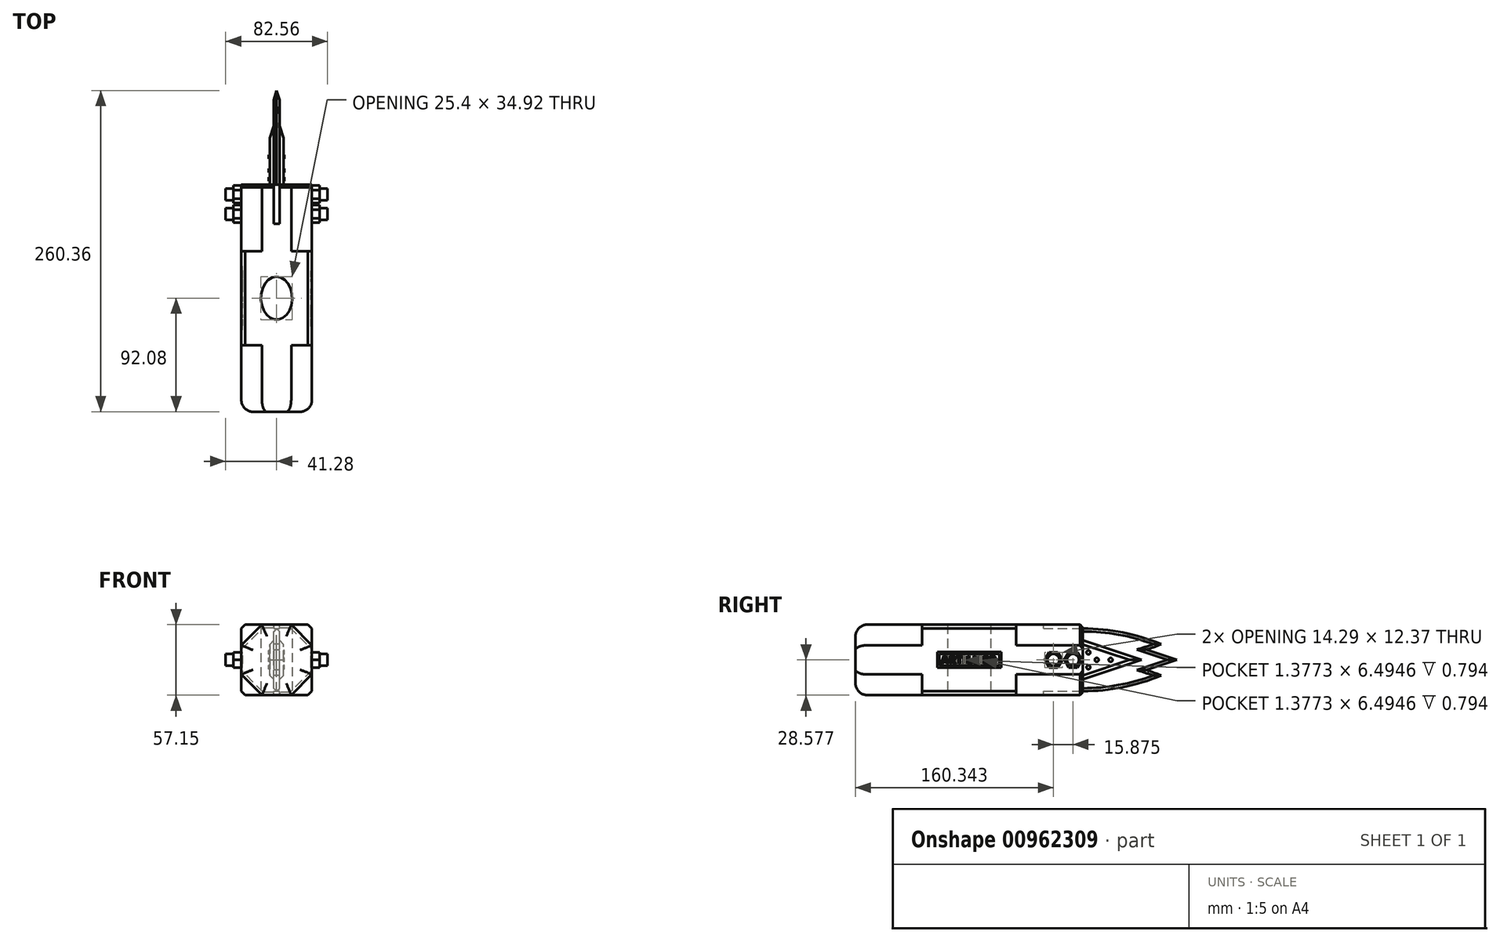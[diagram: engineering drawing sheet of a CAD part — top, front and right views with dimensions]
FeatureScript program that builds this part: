
annotation { "Feature Type Name" : "Feature", "Feature Type Description" : "" }
export const myFeature = defineFeature(function(context is Context, id is Id, definition is map)
    precondition{}
    {
        {
            var Q0;
            Q0=qCreatedBy(makeId("Top.planeOp"),FACE);
            var sketch = newSketch(context, id + "F0", { "sketchPlane" : qUnion([Q0])});
            skEllipse(sketch, "E0", {"center": v(0, 0) * mm, "majorRadius": 12.7 * mm, "minorRadius": 17.46 * mm, "majorAxis": v(1, 0)});
            skSolve(sketch);
        }
        {
            var Q0;
            Q0=qSketchRegion(id+"F0",true);
            extrude(context, id + "F1", {"entities" : qUnion([Q0]), "depth" : 1219.2 * mm, "offsetDistance" : 25.4 * mm});
        }
        {
            var Q0;
            Q0=qCreatedBy(makeId("Front.planeOp"),FACE);
            var sketch = newSketch(context, id + "F2", { "sketchPlane" : qUnion([Q0])});
            skCircle(sketch, "E1.cCircle", {"center": v(0, 1177.87) * mm, "radius": 30.93 * mm, "construction": true});
            skLineSegment(sketch, "E1.0", {"start": v(28.57, 1189.7) * mm, "end": v(28.57, 1166.03) * mm});
            skLineSegment(sketch, "E1.1", {"start": v(28.57, 1166.03) * mm, "end": v(11.84, 1149.3) * mm});
            skLineSegment(sketch, "E1.2", {"start": v(11.84, 1149.3) * mm, "end": v(-11.84, 1149.3) * mm});
            skLineSegment(sketch, "E1.3", {"start": v(-11.84, 1149.3) * mm, "end": v(-28.58, 1166.03) * mm});
            skLineSegment(sketch, "E1.4", {"start": v(-28.58, 1166.03) * mm, "end": v(-28.58, 1189.7) * mm});
            skLineSegment(sketch, "E1.5", {"start": v(-28.57, 1189.7) * mm, "end": v(-11.84, 1206.44) * mm});
            skLineSegment(sketch, "E1.6", {"start": v(-11.84, 1206.44) * mm, "end": v(11.84, 1206.44) * mm});
            skLineSegment(sketch, "E1.7", {"start": v(11.84, 1206.44) * mm, "end": v(28.57, 1189.7) * mm});
            skLineSegment(sketch, "E2.bottom", {"start": v(28.57, 1206.44) * mm, "end": v(-28.58, 1206.44) * mm});
            skLineSegment(sketch, "E2.top", {"start": v(28.57, 1149.3) * mm, "end": v(-28.58, 1149.3) * mm});
            skLineSegment(sketch, "E2.left", {"start": v(28.57, 1206.44) * mm, "end": v(28.57, 1149.3) * mm});
            skLineSegment(sketch, "E2.right", {"start": v(-28.58, 1206.44) * mm, "end": v(-28.58, 1149.3) * mm});
            skSolve(sketch);
        }
        {
            var Q0;
            {var subQ0=sQuery(id+"F2.wireOp",EDGE,"E1.5");Q0=makeQuery(id+"F2.imprint","IMPRINT",FACE,{"disambiguationData":[TD([[makeQuery(id+"F2.imprint","IMPRINT",EDGE,{"derivedFrom":subQ0}),1.0]])]});}
            var Q1;
            {var subQ0=sQuery(id+"F2.wireOp",EDGE,"E1.7");Q1=makeQuery(id+"F2.imprint","IMPRINT",FACE,{"disambiguationData":[TD([[makeQuery(id+"F2.imprint","IMPRINT",EDGE,{"derivedFrom":subQ0}),1.0]])]});}
            var Q2;
            Q2=makeQuery(id+"F2.imprint","IMPRINT",FACE,{"disambiguationData":[TD([[makeQuery(id+"F2.imprint","IMPRINT",EDGE,{"derivedFrom":sQuery(id+"F2.wireOp",EDGE,"E1.0")}),-1.0]])]});
            var Q3;
            {var subQ0=sQuery(id+"F2.wireOp",EDGE,"E1.3");Q3=makeQuery(id+"F2.imprint","IMPRINT",FACE,{"disambiguationData":[TD([[makeQuery(id+"F2.imprint","IMPRINT",EDGE,{"derivedFrom":subQ0}),1.0]])]});}
            var Q4;
            {var subQ0=sQuery(id+"F2.wireOp",EDGE,"E1.1");Q4=makeQuery(id+"F2.imprint","IMPRINT",FACE,{"disambiguationData":[TD([[makeQuery(id+"F2.imprint","IMPRINT",EDGE,{"derivedFrom":subQ0}),1.0]])]});}
            extrude(context, id + "F3", {"entities" : qUnion([Q0, Q1, Q2, Q3, Q4]), "depth" : 38.1 * mm, "offsetDistance" : 25.4 * mm, "hasSecondDirection" : true, "secondDirectionOppositeDirection" : true, "secondDirectionDepth" : 38.1 * mm});
        }
        {
            var Q0;
            Q0=makeQuery(id+"F2.imprint","IMPRINT",FACE,{"disambiguationData":[TD([[makeQuery(id+"F2.imprint","IMPRINT",EDGE,{"derivedFrom":sQuery(id+"F2.wireOp",EDGE,"E1.0")}),-1.0]])]});
            extrude(context, id + "F4", {"entities" : qUnion([Q0]), "operationType" : NewBodyOperationType.ADD, "depth" : 92.07 * mm, "offsetDistance" : 25.4 * mm, "hasSecondDirection" : true, "secondDirectionOppositeDirection" : true, "secondDirectionDepth" : 92.07 * mm});
        }
        {
            var Q0;
            Q0=makeQuery(id+"F4.opExtrude","CAP_FACE",FACE,{"disambiguationData":[OSD([sQuery(id+"F2.wireOp",EDGE,"E1.0"),sQuery(id+"F2.wireOp",EDGE,"E1.1"),sQuery(id+"F2.wireOp",EDGE,"E1.2"),sQuery(id+"F2.wireOp",EDGE,"E1.3"),sQuery(id+"F2.wireOp",EDGE,"E1.4"),sQuery(id+"F2.wireOp",EDGE,"E1.5"),sQuery(id+"F2.wireOp",EDGE,"E1.6"),sQuery(id+"F2.wireOp",EDGE,"E1.7")])],"isStart":false});
            fillet(context, id + "F5", {"entities" : qUnion([Q0]), "radius" : 9.52 * mm, "tangentPropagation" : true, "allowEdgeOverflow" : false});
        }
        {
            var Q0;
            Q0=makeQuery(id+"F3.opExtrude","SWEPT_EDGE",EDGE,{"disambiguationData":[OSD([sQuery(id+"F2.wireOp",EDGE,"E2.bottom"),sQuery(id+"F2.wireOp",EDGE,"E2.left")])]});
            var Q1;
            Q1=makeQuery(id+"F3.opExtrude","SWEPT_EDGE",EDGE,{"disambiguationData":[OSD([sQuery(id+"F2.wireOp",EDGE,"E2.top"),sQuery(id+"F2.wireOp",EDGE,"E2.left")])]});
            var Q2;
            Q2=makeQuery(id+"F3.opExtrude","SWEPT_EDGE",EDGE,{"disambiguationData":[OSD([sQuery(id+"F2.wireOp",EDGE,"E2.bottom"),sQuery(id+"F2.wireOp",EDGE,"E2.right")])]});
            var Q3;
            Q3=makeQuery(id+"F3.opExtrude","SWEPT_EDGE",EDGE,{"disambiguationData":[OSD([sQuery(id+"F2.wireOp",EDGE,"E2.top"),sQuery(id+"F2.wireOp",EDGE,"E2.right")])]});
            chamfer(context, id + "F6", {"entities" : qUnion([Q0, Q1, Q2, Q3]), "width" : 3.17 * mm, "tangentPropagation" : true});
        }
        {
            var Q0;
            Q0=qSketchRegion(id+"F0",true);
            extrude(context, id + "F7", {"entities" : qUnion([Q0]), "operationType" : NewBodyOperationType.REMOVE, "depth" : 1219.2 * mm, "offsetDistance" : 25.4 * mm});
        }
        {
            var Q0;
            {var subQ0=sQuery(id+"F2.wireOp",EDGE,"E1.0");Q0=makeQuery(id+"F4.boolean.opBoolean","MERGE",FACE,{"derivedFrom":[makeQuery(id+"F3.opExtrude","SWEPT_FACE",FACE,{"disambiguationData":[OSD([subQ0,sQuery(id+"F2.wireOp",EDGE,"E2.left")])]}),makeQuery(id+"F4.opExtrude","SWEPT_FACE",FACE,{"disambiguationData":[OSD([subQ0])]})]});}
            var sketch = newSketch(context, id + "F8", { "sketchPlane" : qUnion([Q0])});
            skLineSegment(sketch, "E3.bottom", {"start": v(28.57, 1162) * mm, "end": v(-28.58, 1162) * mm, "construction": true});
            skLineSegment(sketch, "E3.top", {"start": v(28.57, 1193.74) * mm, "end": v(-28.58, 1193.74) * mm, "construction": true});
            skLineSegment(sketch, "E3.left", {"start": v(28.57, 1162) * mm, "end": v(28.57, 1193.74) * mm, "construction": true});
            skLineSegment(sketch, "E3.right", {"start": v(-28.57, 1162) * mm, "end": v(-28.57, 1193.74) * mm, "construction": true});
            skPoint(sketch, "E3.middle", {"position": v(0, 1177.87) * mm});
            skLineSegment(sketch, "E4", {"start": v(0, 1193.74) * mm, "end": v(-28.58, 1177.87) * mm, "construction": true});
            skLineSegment(sketch, "E5", {"start": v(-28.57, 1177.87) * mm, "end": v(0, 1162) * mm, "construction": true});
            skLineSegment(sketch, "E6", {"start": v(0, 1162) * mm, "end": v(28.58, 1177.87) * mm, "construction": true});
            skLineSegment(sketch, "E7", {"start": v(28.58, 1177.87) * mm, "end": v(0, 1193.74) * mm, "construction": true});
            skLineSegment(sketch, "E8.bottom", {"start": v(24.29, 1173.01) * mm, "end": v(-24.29, 1173.01) * mm});
            skLineSegment(sketch, "E8.top", {"start": v(24.29, 1182.72) * mm, "end": v(-24.29, 1182.72) * mm});
            skLineSegment(sketch, "E8.left", {"start": v(24.29, 1173.01) * mm, "end": v(24.29, 1182.72) * mm});
            skLineSegment(sketch, "E8.right", {"start": v(-24.29, 1173.01) * mm, "end": v(-24.29, 1182.72) * mm});
            skLineSegment(sketch, "E9.bottom", {"start": v(25.87, 1171.43) * mm, "end": v(-25.87, 1171.43) * mm});
            skLineSegment(sketch, "E9.top", {"start": v(25.87, 1184.3) * mm, "end": v(-25.87, 1184.3) * mm});
            skLineSegment(sketch, "E9.left", {"start": v(25.87, 1171.43) * mm, "end": v(25.87, 1184.3) * mm});
            skLineSegment(sketch, "E9.right", {"start": v(-25.87, 1171.43) * mm, "end": v(-25.87, 1184.3) * mm});
            skPoint(sketch, "E10.sketch_text.left.end.orphan", {"position": v(-22.7, 1181.13) * mm});
            skPoint(sketch, "E11", {"position": v(22.7, 1181.13) * mm});
            skPoint(sketch, "E12", {"position": v(22.7, 1174.6) * mm});
            skPoint(sketch, "E13", {"position": v(-22.7, 1174.6) * mm});
            skText(sketch, "E14", { "text": "ARTILLIER", "fontName": "OpenSans-Bold.ttf"});
            const initialGuessF8  = {"E14": [-0.02283, 1.1746, 1, 0, 0.00655]};
            skSetInitialGuess(sketch, initialGuessF8);
            skSolve(sketch);
        }
        {
            var Q0;
            Q0=makeQuery(id+"F8.imprint","IMPRINT",FACE,{"disambiguationData":[TD([[makeQuery(id+"F8.imprint","IMPRINT",EDGE,{"derivedFrom":sQuery(id+"F8.wireOp",EDGE,"E14.sketch_text.stroke-0")}),-1.0]])]});
            var Q1;
            Q1=makeQuery(id+"F8.imprint","IMPRINT",FACE,{"disambiguationData":[TD([[makeQuery(id+"F8.imprint","IMPRINT",EDGE,{"derivedFrom":sQuery(id+"F8.wireOp",EDGE,"E14.sketch_text.stroke-12")}),-1.0]])]});
            var Q2;
            Q2=makeQuery(id+"F8.imprint","IMPRINT",FACE,{"disambiguationData":[TD([[makeQuery(id+"F8.imprint","IMPRINT",EDGE,{"derivedFrom":sQuery(id+"F8.wireOp",EDGE,"E14.sketch_text.stroke-31")}),-1.0]])]});
            var Q3;
            Q3=makeQuery(id+"F8.imprint","IMPRINT",FACE,{"disambiguationData":[TD([[makeQuery(id+"F8.imprint","IMPRINT",EDGE,{"derivedFrom":sQuery(id+"F8.wireOp",EDGE,"E14.sketch_text.stroke-39")}),-1.0]])]});
            var Q4;
            Q4=makeQuery(id+"F8.imprint","IMPRINT",FACE,{"disambiguationData":[TD([[makeQuery(id+"F8.imprint","IMPRINT",EDGE,{"derivedFrom":sQuery(id+"F8.wireOp",EDGE,"E14.sketch_text.stroke-43")}),-1.0]])]});
            var Q5;
            Q5=makeQuery(id+"F8.imprint","IMPRINT",FACE,{"disambiguationData":[TD([[makeQuery(id+"F8.imprint","IMPRINT",EDGE,{"derivedFrom":sQuery(id+"F8.wireOp",EDGE,"E8.bottom")}),1.0]])]});
            var Q6;
            Q6=makeQuery(id+"F8.imprint","IMPRINT",FACE,{"disambiguationData":[TD([[makeQuery(id+"F8.imprint","IMPRINT",EDGE,{"derivedFrom":sQuery(id+"F8.wireOp",EDGE,"E14.sketch_text.stroke-49")}),-1.0]])]});
            var Q7;
            Q7=makeQuery(id+"F8.imprint","IMPRINT",FACE,{"disambiguationData":[TD([[makeQuery(id+"F8.imprint","IMPRINT",EDGE,{"derivedFrom":sQuery(id+"F8.wireOp",EDGE,"E14.sketch_text.stroke-55")}),-1.0]])]});
            var Q8;
            Q8=makeQuery(id+"F8.imprint","IMPRINT",FACE,{"disambiguationData":[TD([[makeQuery(id+"F8.imprint","IMPRINT",EDGE,{"derivedFrom":sQuery(id+"F8.wireOp",EDGE,"E14.sketch_text.stroke-59")}),-1.0]])]});
            var Q9;
            Q9=makeQuery(id+"F8.imprint","IMPRINT",FACE,{"disambiguationData":[TD([[makeQuery(id+"F8.imprint","IMPRINT",EDGE,{"derivedFrom":sQuery(id+"F8.wireOp",EDGE,"E14.sketch_text.stroke-71")}),-1.0]])]});
            extrude(context, id + "F9", {"entities" : qUnion([Q0, Q1, Q2, Q3, Q4, Q5, Q6, Q7, Q8, Q9]), "operationType" : NewBodyOperationType.REMOVE, "oppositeDirection" : true, "depth" : 0.8 * mm, "offsetDistance" : 25.4 * mm});
        }
        {
            var Q0;
            {var subQ0=sQuery(id+"F2.wireOp",EDGE,"E1.4");Q0=makeQuery(id+"F4.boolean.opBoolean","MERGE",FACE,{"derivedFrom":[makeQuery(id+"F3.opExtrude","SWEPT_FACE",FACE,{"disambiguationData":[OSD([subQ0,sQuery(id+"F2.wireOp",EDGE,"E2.right")])]}),makeQuery(id+"F4.opExtrude","SWEPT_FACE",FACE,{"disambiguationData":[OSD([subQ0])]})]});}
            var sketch = newSketch(context, id + "F10", { "sketchPlane" : qUnion([Q0])});
            skLineSegment(sketch, "E15.bottom", {"start": v(28.57, 1162.05) * mm, "end": v(-28.57, 1162.05) * mm, "construction": true});
            skLineSegment(sketch, "E15.top", {"start": v(28.57, 1193.8) * mm, "end": v(-28.57, 1193.8) * mm, "construction": true});
            skLineSegment(sketch, "E15.left", {"start": v(28.57, 1162.05) * mm, "end": v(28.57, 1193.8) * mm, "construction": true});
            skLineSegment(sketch, "E15.right", {"start": v(-28.57, 1162.05) * mm, "end": v(-28.57, 1193.8) * mm, "construction": true});
            skPoint(sketch, "E15.middle", {"position": v(0, 1177.93) * mm});
            skLineSegment(sketch, "E16", {"start": v(0, 1193.8) * mm, "end": v(-28.57, 1177.93) * mm, "construction": true});
            skLineSegment(sketch, "E17", {"start": v(-28.57, 1177.93) * mm, "end": v(0, 1162.05) * mm, "construction": true});
            skLineSegment(sketch, "E18", {"start": v(0, 1162.05) * mm, "end": v(28.57, 1177.93) * mm, "construction": true});
            skLineSegment(sketch, "E19", {"start": v(28.57, 1177.93) * mm, "end": v(0, 1193.8) * mm, "construction": true});
            skLineSegment(sketch, "E20.bottom", {"start": v(24.29, 1173.07) * mm, "end": v(-24.29, 1173.07) * mm});
            skLineSegment(sketch, "E20.top", {"start": v(24.29, 1182.78) * mm, "end": v(-24.29, 1182.78) * mm});
            skLineSegment(sketch, "E20.left", {"start": v(24.29, 1173.07) * mm, "end": v(24.29, 1182.78) * mm});
            skLineSegment(sketch, "E20.right", {"start": v(-24.29, 1173.07) * mm, "end": v(-24.29, 1182.78) * mm});
            skLineSegment(sketch, "E21.bottom", {"start": v(25.87, 1171.49) * mm, "end": v(-25.87, 1171.49) * mm});
            skLineSegment(sketch, "E21.top", {"start": v(25.87, 1184.36) * mm, "end": v(-25.87, 1184.36) * mm});
            skLineSegment(sketch, "E21.left", {"start": v(25.87, 1171.49) * mm, "end": v(25.87, 1184.36) * mm});
            skLineSegment(sketch, "E21.right", {"start": v(-25.87, 1171.49) * mm, "end": v(-25.87, 1184.36) * mm});
            skPoint(sketch, "E22.sketch_text.left.end.orphan", {"position": v(-22.7, 1181.19) * mm});
            skText(sketch, "E23", { "text": "ARTILLIER", "fontName": "OpenSans-Bold.ttf"});
            const initialGuessF10  = {"E23": [-0.02243, 1.17481, 1, 0, 0.00653]};
            skSetInitialGuess(sketch, initialGuessF10);
            skSolve(sketch);
        }
        {
            var Q0;
            Q0=makeQuery(id+"F10.imprint","IMPRINT",FACE,{"disambiguationData":[TD([[makeQuery(id+"F10.imprint","IMPRINT",EDGE,{"derivedFrom":sQuery(id+"F10.wireOp",EDGE,"E20.bottom")}),1.0]])]});
            var Q1;
            Q1=makeQuery(id+"F10.imprint","IMPRINT",FACE,{"disambiguationData":[TD([[makeQuery(id+"F10.imprint","IMPRINT",EDGE,{"derivedFrom":sQuery(id+"F10.wireOp",EDGE,"E23.sketch_text.stroke-0")}),-1.0]])]});
            var Q2;
            Q2=makeQuery(id+"F10.imprint","IMPRINT",FACE,{"disambiguationData":[TD([[makeQuery(id+"F10.imprint","IMPRINT",EDGE,{"derivedFrom":sQuery(id+"F10.wireOp",EDGE,"E23.sketch_text.stroke-12")}),-1.0]])]});
            var Q3;
            Q3=makeQuery(id+"F10.imprint","IMPRINT",FACE,{"disambiguationData":[TD([[makeQuery(id+"F10.imprint","IMPRINT",EDGE,{"derivedFrom":sQuery(id+"F10.wireOp",EDGE,"E23.sketch_text.stroke-39")}),-1.0]])]});
            var Q4;
            Q4=makeQuery(id+"F10.imprint","IMPRINT",FACE,{"disambiguationData":[TD([[makeQuery(id+"F10.imprint","IMPRINT",EDGE,{"derivedFrom":sQuery(id+"F10.wireOp",EDGE,"E23.sketch_text.stroke-43")}),-1.0]])]});
            var Q5;
            Q5=makeQuery(id+"F10.imprint","IMPRINT",FACE,{"disambiguationData":[TD([[makeQuery(id+"F10.imprint","IMPRINT",EDGE,{"derivedFrom":sQuery(id+"F10.wireOp",EDGE,"E23.sketch_text.stroke-31")}),-1.0]])]});
            var Q6;
            Q6=makeQuery(id+"F10.imprint","IMPRINT",FACE,{"disambiguationData":[TD([[makeQuery(id+"F10.imprint","IMPRINT",EDGE,{"derivedFrom":sQuery(id+"F10.wireOp",EDGE,"E23.sketch_text.stroke-55")}),-1.0]])]});
            var Q7;
            Q7=makeQuery(id+"F10.imprint","IMPRINT",FACE,{"disambiguationData":[TD([[makeQuery(id+"F10.imprint","IMPRINT",EDGE,{"derivedFrom":sQuery(id+"F10.wireOp",EDGE,"E23.sketch_text.stroke-59")}),-1.0]])]});
            var Q8;
            Q8=makeQuery(id+"F10.imprint","IMPRINT",FACE,{"disambiguationData":[TD([[makeQuery(id+"F10.imprint","IMPRINT",EDGE,{"derivedFrom":sQuery(id+"F10.wireOp",EDGE,"E23.sketch_text.stroke-71")}),-1.0]])]});
            var Q9;
            Q9=makeQuery(id+"F10.imprint","IMPRINT",FACE,{"disambiguationData":[TD([[makeQuery(id+"F10.imprint","IMPRINT",EDGE,{"derivedFrom":sQuery(id+"F10.wireOp",EDGE,"E23.sketch_text.stroke-49")}),-1.0]])]});
            extrude(context, id + "F11", {"entities" : qUnion([Q0, Q1, Q2, Q3, Q4, Q5, Q6, Q7, Q8, Q9]), "operationType" : NewBodyOperationType.REMOVE, "oppositeDirection" : true, "depth" : 0.8 * mm, "offsetDistance" : 25.4 * mm});
        }
        {
            var Q0;
            {var subQ1=sQuery(id+"F2.wireOp",EDGE,"E1.1");var subQ3=sQuery(id+"F2.wireOp",EDGE,"E2.left");var subQ9=sQuery(id+"F2.wireOp",EDGE,"E1.0");Q0=makeQuery(id+"F9.boolean.opBoolean","SPLIT",FACE,{"disambiguationData":[TD([makeQuery(id+"F4.opExtrude","SWEPT_FACE",FACE,{"disambiguationData":[OSD([subQ1])]})])],"derivedFrom":makeQuery(id+"F4.boolean.opBoolean","MERGE",FACE,{"derivedFrom":[makeQuery(id+"F3.opExtrude","SWEPT_FACE",FACE,{"disambiguationData":[OSD([subQ9,subQ3])]}),makeQuery(id+"F4.opExtrude","SWEPT_FACE",FACE,{"disambiguationData":[OSD([subQ9])]})]})});}
            var sketch = newSketch(context, id + "F12", { "sketchPlane" : qUnion([Q0])});
            skPoint(sketch, "E24", {"position": v(92.08, 1177.87) * mm});
            skLineSegment(sketch, "E25.bottom", {"start": v(60.32, 1203.27) * mm, "end": v(155.57, 1203.27) * mm});
            skLineSegment(sketch, "E25.top", {"start": v(60.32, 1152.47) * mm, "end": v(155.57, 1152.47) * mm});
            skLineSegment(sketch, "E25.left", {"start": v(60.32, 1203.27) * mm, "end": v(60.32, 1152.47) * mm});
            skLineSegment(sketch, "E25.right", {"start": v(155.57, 1203.27) * mm, "end": v(155.57, 1152.47) * mm, "construction": true});
            skPoint(sketch, "E26", {"position": v(155.58, 1190.57) * mm});
            skPoint(sketch, "E27", {"position": v(155.58, 1165.17) * mm});
            skArc(sketch, "E28", {"start": v(155.58, 1190.57) * mm, "mid": v(124.45, 1200.06) * mm, "end": v(92.07, 1203.27) * mm});
            skArc(sketch, "E29", {"start": v(92.07, 1152.47) * mm, "mid": v(124.45, 1155.67) * mm, "end": v(155.57, 1165.17) * mm});
            skArc(sketch, "E30", {"start": v(155.58, 1165.17) * mm, "mid": v(124.45, 1174.66) * mm, "end": v(92.08, 1177.87) * mm});
            skArc(sketch, "E31", {"start": v(92.07, 1177.87) * mm, "mid": v(124.45, 1181.07) * mm, "end": v(155.57, 1190.57) * mm});
            skLineSegment(sketch, "E32", {"start": v(92.08, 1177.87) * mm, "end": v(60.32, 1177.87) * mm, "construction": true});
            skLineSegment(sketch, "E33", {"start": v(92.08, 1203.27) * mm, "end": v(92.07, 1152.47) * mm});
            skSolve(sketch);
        }
        {
            var Q0;
            {var subQ11=sQuery(id+"F12.wireOp",EDGE,"E28");Q0=makeQuery(id+"F12.imprint","IMPRINT",FACE,{"disambiguationData":[TD([[makeQuery(id+"F12.imprint","IMPRINT",EDGE,{"derivedFrom":subQ11}),1.0]])]});}
            var Q1;
            {var subQ11=sQuery(id+"F12.wireOp",EDGE,"E29");Q1=makeQuery(id+"F12.imprint","IMPRINT",FACE,{"disambiguationData":[TD([[makeQuery(id+"F12.imprint","IMPRINT",EDGE,{"derivedFrom":subQ11}),1.0]])]});}
            var Q2;
            {var subQ1=sQuery(id+"F2.wireOp",EDGE,"E2.left");var subQ11=makeQuery(id+"F4.opExtrude","CAP_EDGE",EDGE,{"disambiguationData":[OSD([subQ1])],"isStart":true});var subQ17=makeQuery(id+"F12.imprint","INTERSECT",VERTEX,{"derivedFrom":[subQ11,sQuery(id+"F12.wireOp",EDGE,"E30"),sQuery(id+"F12.wireOp",EDGE,"E31")]});Q2=makeQuery(id+"F12.imprint","IMPRINT",FACE,{"disambiguationData":[TD([[makeQuery(id+"F12.imprint","IMPRINT",EDGE,{"disambiguationData":[TD([[subQ17,-1.0]])],"derivedFrom":subQ11}),-1.0]])]});}
            extrude(context, id + "F13", {"entities" : qUnion([Q0, Q1, Q2]), "oppositeDirection" : true, "depth" : 30.96 * mm, "offsetDistance" : 25.4 * mm, "hasSecondDirection" : true, "secondDirectionOppositeDirection" : true, "secondDirectionDepth" : 26.2 * mm});
        }
        {
            var Q0;
            Q0=makeQuery(id+"F4.opExtrude","CAP_FACE",FACE,{"disambiguationData":[OSD([sQuery(id+"F2.wireOp",EDGE,"E1.0"),sQuery(id+"F2.wireOp",EDGE,"E1.1"),sQuery(id+"F2.wireOp",EDGE,"E1.2"),sQuery(id+"F2.wireOp",EDGE,"E1.3"),sQuery(id+"F2.wireOp",EDGE,"E1.4"),sQuery(id+"F2.wireOp",EDGE,"E1.5"),sQuery(id+"F2.wireOp",EDGE,"E1.6"),sQuery(id+"F2.wireOp",EDGE,"E1.7")])],"isStart":true});
            var sketch = newSketch(context, id + "F14", { "sketchPlane" : qUnion([Q0])});
            skLineSegment(sketch, "E34.bottom", {"start": v(2.38, 1149.3) * mm, "end": v(-2.38, 1149.3) * mm});
            skLineSegment(sketch, "E34.top", {"start": v(2.38, 1206.44) * mm, "end": v(-2.38, 1206.44) * mm});
            skLineSegment(sketch, "E34.left", {"start": v(2.38, 1149.3) * mm, "end": v(2.38, 1206.44) * mm});
            skLineSegment(sketch, "E34.right", {"start": v(-2.38, 1149.3) * mm, "end": v(-2.38, 1206.44) * mm});
            skPoint(sketch, "E34.middle", {"position": v(0, 1177.87) * mm});
            skSolve(sketch);
        }
        {
            var Q0;
            Q0 = qSketchRegion(id + "F14", true);
            extrude(context, id + "F15", {"entities" : qUnion([Q0]), "operationType" : NewBodyOperationType.REMOVE, "oppositeDirection" : true, "depth" : 31.75 * mm, "offsetDistance" : 25.4 * mm});
        }
        {
            var Q0;
            {var subQ1=sQuery(id+"F2.wireOp",EDGE,"E1.1");var subQ3=sQuery(id+"F2.wireOp",EDGE,"E2.left");var subQ9=sQuery(id+"F2.wireOp",EDGE,"E1.0");Q0=makeQuery(id+"F9.boolean.opBoolean","SPLIT",FACE,{"disambiguationData":[TD([makeQuery(id+"F4.opExtrude","SWEPT_FACE",FACE,{"disambiguationData":[OSD([subQ1])]})])],"derivedFrom":makeQuery(id+"F4.boolean.opBoolean","MERGE",FACE,{"derivedFrom":[makeQuery(id+"F3.opExtrude","SWEPT_FACE",FACE,{"disambiguationData":[OSD([subQ9,subQ3])]}),makeQuery(id+"F4.opExtrude","SWEPT_FACE",FACE,{"disambiguationData":[OSD([subQ9])]})]})});}
            var sketch = newSketch(context, id + "F16", { "sketchPlane" : qUnion([Q0])});
            skCircle(sketch, "E35", {"center": v(84.14, 1177.87) * mm, "radius": 4.76 * mm});
            skPoint(sketch, "E35.centerSnap0", {"position": v(92.08, 1177.87) * mm});
            skCircle(sketch, "E36", {"center": v(68.26, 1177.87) * mm, "radius": 4.76 * mm});
            skPoint(sketch, "E37", {"position": v(60.33, 1177.87) * mm});
            skCircle(sketch, "E38.cCircle", {"center": v(84.14, 1177.87) * mm, "radius": 6.19 * mm, "construction": true});
            skLineSegment(sketch, "E38.0", {"start": v(87.7, 1171.68) * mm, "end": v(80.57, 1171.68) * mm});
            skLineSegment(sketch, "E38.1", {"start": v(80.57, 1171.68) * mm, "end": v(77, 1177.87) * mm});
            skLineSegment(sketch, "E38.2", {"start": v(77, 1177.87) * mm, "end": v(80.57, 1184.05) * mm});
            skLineSegment(sketch, "E38.3", {"start": v(80.57, 1184.05) * mm, "end": v(87.7, 1184.05) * mm});
            skLineSegment(sketch, "E38.4", {"start": v(87.7, 1184.05) * mm, "end": v(91.28, 1177.87) * mm});
            skLineSegment(sketch, "E38.5", {"start": v(91.28, 1177.87) * mm, "end": v(87.7, 1171.68) * mm});
            skPoint(sketch, "E38.0.midPoint", {"position": v(84.14, 1171.68) * mm});
            skCircle(sketch, "E39.cCircle", {"center": v(68.26, 1177.87) * mm, "radius": 6.19 * mm, "construction": true});
            skLineSegment(sketch, "E39.0", {"start": v(71.83, 1171.68) * mm, "end": v(64.7, 1171.68) * mm});
            skLineSegment(sketch, "E39.1", {"start": v(64.7, 1171.68) * mm, "end": v(61.12, 1177.87) * mm});
            skLineSegment(sketch, "E39.2", {"start": v(61.12, 1177.87) * mm, "end": v(64.7, 1184.05) * mm});
            skLineSegment(sketch, "E39.3", {"start": v(64.7, 1184.05) * mm, "end": v(71.83, 1184.05) * mm});
            skLineSegment(sketch, "E39.4", {"start": v(71.83, 1184.05) * mm, "end": v(75.4, 1177.87) * mm});
            skLineSegment(sketch, "E39.5", {"start": v(75.4, 1177.87) * mm, "end": v(71.83, 1171.68) * mm});
            skPoint(sketch, "E39.0.midPoint", {"position": v(68.26, 1171.68) * mm});
            skSolve(sketch);
        }
        {
            var Q0;
            Q0=makeQuery(id+"F16.imprint","IMPRINT",FACE,{"disambiguationData":[TD([[makeQuery(id+"F16.imprint","IMPRINT",EDGE,{"derivedFrom":sQuery(id+"F16.wireOp",EDGE,"E36")}),1.0]])]});
            var Q1;
            Q1=makeQuery(id+"F16.imprint","IMPRINT",FACE,{"disambiguationData":[TD([[makeQuery(id+"F16.imprint","IMPRINT",EDGE,{"derivedFrom":sQuery(id+"F16.wireOp",EDGE,"E35")}),1.0]])]});
            extrude(context, id + "F17", {"entities" : qUnion([Q0, Q1]), "oppositeDirection" : true, "depth" : 69.85 * mm, "offsetDistance" : 25.4 * mm, "hasSecondDirection" : true, "secondDirectionOppositeDirection" : false, "secondDirectionDepth" : 12.7 * mm});
        }
        {
            var Q0;
            Q0=makeQuery(id+"F16.imprint","IMPRINT",FACE,{"disambiguationData":[TD([[makeQuery(id+"F16.imprint","IMPRINT",EDGE,{"derivedFrom":sQuery(id+"F16.wireOp",EDGE,"E36")}),-1.0]])]});
            var Q1;
            Q1=makeQuery(id+"F16.imprint","IMPRINT",FACE,{"disambiguationData":[TD([[makeQuery(id+"F16.imprint","IMPRINT",EDGE,{"derivedFrom":sQuery(id+"F16.wireOp",EDGE,"E35")}),-1.0]])]});
            extrude(context, id + "F18", {"entities" : qUnion([Q0, Q1]), "operationType" : NewBodyOperationType.ADD, "depth" : 6.35 * mm, "offsetDistance" : 25.4 * mm});
        }
        {
            var Q0;
            Q0=makeQuery(id+"F16.imprint","IMPRINT",FACE,{"disambiguationData":[TD([[makeQuery(id+"F16.imprint","IMPRINT",EDGE,{"derivedFrom":sQuery(id+"F16.wireOp",EDGE,"E35")}),-1.0]])]});
            var Q1;
            Q1=makeQuery(id+"F16.imprint","IMPRINT",FACE,{"disambiguationData":[TD([[makeQuery(id+"F16.imprint","IMPRINT",EDGE,{"derivedFrom":sQuery(id+"F16.wireOp",EDGE,"E36")}),-1.0]])]});
            extrude(context, id + "F19", {"entities" : qUnion([Q0, Q1]), "operationType" : NewBodyOperationType.ADD, "oppositeDirection" : true, "depth" : 63.5 * mm, "offsetDistance" : 25.4 * mm, "hasSecondDirection" : true, "secondDirectionOppositeDirection" : true, "secondDirectionDepth" : 57.15 * mm});
        }
        {
            var Q0;
            Q0=makeQuery(id+"F13.opExtrude","CAP_EDGE",EDGE,{"disambiguationData":[OSD([sQuery(id+"F12.wireOp",EDGE,"E28")])],"isStart":true});
            var Q1;
            Q1=makeQuery(id+"F13.opExtrude","CAP_EDGE",EDGE,{"disambiguationData":[OSD([sQuery(id+"F12.wireOp",EDGE,"E28")])],"isStart":false});
            var Q2;
            Q2=makeQuery(id+"F13.opExtrude","CAP_EDGE",EDGE,{"disambiguationData":[OSD([sQuery(id+"F12.wireOp",EDGE,"E29")])],"isStart":false});
            var Q3;
            Q3=makeQuery(id+"F13.opExtrude","CAP_EDGE",EDGE,{"disambiguationData":[OSD([sQuery(id+"F12.wireOp",EDGE,"E29")])],"isStart":true});
            var Q4;
            Q4=makeQuery(id+"F15.boolean.opBoolean","COPY",EDGE,{"derivedFrom":makeQuery(id+"F15.opExtrude","SWEPT_EDGE",EDGE,{"disambiguationData":[OSD([sQuery(id+"F2.wireOp",EDGE,"E1.6"),sQuery(id+"F14.wireOp",EDGE,"E34.top"),sQuery(id+"F14.wireOp",EDGE,"E34.left")])]})});
            var Q5;
            Q5=makeQuery(id+"F15.boolean.opBoolean","COPY",EDGE,{"derivedFrom":makeQuery(id+"F15.opExtrude","SWEPT_EDGE",EDGE,{"disambiguationData":[OSD([sQuery(id+"F2.wireOp",EDGE,"E1.6"),sQuery(id+"F14.wireOp",EDGE,"E34.top"),sQuery(id+"F14.wireOp",EDGE,"E34.right")])]})});
            var Q6;
            Q6=makeQuery(id+"F15.boolean.opBoolean","COPY",EDGE,{"derivedFrom":makeQuery(id+"F15.opExtrude","CAP_EDGE",EDGE,{"disambiguationData":[OSD([sQuery(id+"F14.wireOp",EDGE,"E34.top")])],"isStart":false})});
            var Q7;
            {var subQ0=sQuery(id+"F2.wireOp",EDGE,"E1.6");var subQ1=sQuery(id+"F2.wireOp",EDGE,"E1.7");Q7=makeQuery(id+"F15.boolean.opBoolean","SPLIT",EDGE,{"disambiguationData":[TD([makeQuery(id+"F4.opExtrude","SWEPT_FACE",FACE,{"disambiguationData":[OSD([subQ1])]})])],"derivedFrom":makeQuery(id+"F4.opExtrude","CAP_EDGE",EDGE,{"disambiguationData":[OSD([subQ0])],"isStart":true})});}
            var Q8;
            {var subQ0=sQuery(id+"F2.wireOp",EDGE,"E1.6");var subQ1=sQuery(id+"F2.wireOp",EDGE,"E1.5");Q8=makeQuery(id+"F15.boolean.opBoolean","SPLIT",EDGE,{"disambiguationData":[TD([makeQuery(id+"F4.opExtrude","SWEPT_FACE",FACE,{"disambiguationData":[OSD([subQ1])]})])],"derivedFrom":makeQuery(id+"F4.opExtrude","CAP_EDGE",EDGE,{"disambiguationData":[OSD([subQ0])],"isStart":true})});}
            var Q9;
            Q9=makeQuery(id+"F4.opExtrude","CAP_EDGE",EDGE,{"disambiguationData":[OSD([sQuery(id+"F2.wireOp",EDGE,"E1.7")])],"isStart":true});
            var Q10;
            Q10=makeQuery(id+"F4.opExtrude","CAP_EDGE",EDGE,{"disambiguationData":[OSD([sQuery(id+"F2.wireOp",EDGE,"E1.5")])],"isStart":true});
            var Q11;
            {var subQ0=sQuery(id+"F2.wireOp",EDGE,"E1.3");var subQ1=sQuery(id+"F2.wireOp",EDGE,"E1.2");Q11=makeQuery(id+"F15.boolean.opBoolean","SPLIT",EDGE,{"disambiguationData":[TD([makeQuery(id+"F4.opExtrude","SWEPT_FACE",FACE,{"disambiguationData":[OSD([subQ0])]})])],"derivedFrom":makeQuery(id+"F4.opExtrude","CAP_EDGE",EDGE,{"disambiguationData":[OSD([subQ1])],"isStart":true})});}
            var Q12;
            Q12=makeQuery(id+"F15.boolean.opBoolean","COPY",EDGE,{"derivedFrom":makeQuery(id+"F15.opExtrude","SWEPT_EDGE",EDGE,{"disambiguationData":[OSD([sQuery(id+"F2.wireOp",EDGE,"E1.2"),sQuery(id+"F14.wireOp",EDGE,"E34.bottom"),sQuery(id+"F14.wireOp",EDGE,"E34.left")])]})});
            var Q13;
            Q13=makeQuery(id+"F15.boolean.opBoolean","COPY",EDGE,{"derivedFrom":makeQuery(id+"F15.opExtrude","CAP_EDGE",EDGE,{"disambiguationData":[OSD([sQuery(id+"F14.wireOp",EDGE,"E34.bottom")])],"isStart":false})});
            var Q14;
            {var subQ0=sQuery(id+"F2.wireOp",EDGE,"E1.2");var subQ1=sQuery(id+"F2.wireOp",EDGE,"E1.1");Q14=makeQuery(id+"F15.boolean.opBoolean","SPLIT",EDGE,{"disambiguationData":[TD([makeQuery(id+"F4.opExtrude","SWEPT_FACE",FACE,{"disambiguationData":[OSD([subQ1])]})])],"derivedFrom":makeQuery(id+"F4.opExtrude","CAP_EDGE",EDGE,{"disambiguationData":[OSD([subQ0])],"isStart":true})});}
            var Q15;
            Q15=makeQuery(id+"F4.opExtrude","CAP_EDGE",EDGE,{"disambiguationData":[OSD([sQuery(id+"F2.wireOp",EDGE,"E1.3")])],"isStart":true});
            var Q16;
            Q16=makeQuery(id+"F15.boolean.opBoolean","COPY",EDGE,{"derivedFrom":makeQuery(id+"F15.opExtrude","SWEPT_EDGE",EDGE,{"disambiguationData":[OSD([sQuery(id+"F2.wireOp",EDGE,"E1.2"),sQuery(id+"F14.wireOp",EDGE,"E34.bottom"),sQuery(id+"F14.wireOp",EDGE,"E34.right")])]})});
            var Q17;
            Q17=makeQuery(id+"F4.opExtrude","CAP_EDGE",EDGE,{"disambiguationData":[OSD([sQuery(id+"F2.wireOp",EDGE,"E1.1")])],"isStart":true});
            var Q18;
            Q18=makeQuery(id+"F13.opExtrude","CAP_EDGE",EDGE,{"disambiguationData":[OSD([sQuery(id+"F12.wireOp",EDGE,"E31")])],"isStart":true});
            var Q19;
            Q19=makeQuery(id+"F13.opExtrude","CAP_EDGE",EDGE,{"disambiguationData":[OSD([sQuery(id+"F12.wireOp",EDGE,"E31")])],"isStart":false});
            var Q20;
            Q20=makeQuery(id+"F13.opExtrude","CAP_EDGE",EDGE,{"disambiguationData":[OSD([sQuery(id+"F12.wireOp",EDGE,"E30")])],"isStart":true});
            var Q21;
            Q21=makeQuery(id+"F13.opExtrude","CAP_EDGE",EDGE,{"disambiguationData":[OSD([sQuery(id+"F12.wireOp",EDGE,"E30")])],"isStart":false});
            chamfer(context, id + "F20", {"entities" : qUnion([Q0, Q1, Q2, Q3, Q4, Q5, Q6, Q7, Q8, Q9, Q10, Q11, Q12, Q13, Q14, Q15, Q16, Q17, Q18, Q19, Q20, Q21]), "width" : 2.38 * mm, "tangentPropagation" : true});
        }
        {
            var Q0;
            {var subQ0=sQuery(id+"F12.wireOp",EDGE,"E25.left");var subQ1=sQuery(id+"F12.wireOp",EDGE,"E25.bottom");var subQ2=makeQuery(id+"F12.imprint","INTERSECT",VERTEX,{"derivedFrom":[subQ1,subQ0]});Q0=makeQuery(id+"F12.imprint","IMPRINT",FACE,{"disambiguationData":[TD([[makeQuery(id+"F12.imprint","IMPRINT",EDGE,{"disambiguationData":[TD([[subQ2,-1.0]])],"derivedFrom":subQ1}),-1.0]])]});}
            var Q1;
            {var subQ0=sQuery(id+"F12.wireOp",EDGE,"E33");var subQ15=makeQuery(id+"F12.imprint","INTERSECT",VERTEX,{"derivedFrom":[sQuery(id+"F12.wireOp",EDGE,"E30"),sQuery(id+"F12.wireOp",EDGE,"E31"),subQ0]});Q1=makeQuery(id+"F12.imprint","IMPRINT",FACE,{"disambiguationData":[TD([[makeQuery(id+"F12.imprint","IMPRINT",EDGE,{"disambiguationData":[TD([[subQ15,1.0]])],"derivedFrom":subQ0}),-1.0]])]});}
            var Q2;
            {var subQ0=sQuery(id+"F12.wireOp",EDGE,"E25.left");var subQ1=sQuery(id+"F12.wireOp",EDGE,"E25.top");var subQ2=makeQuery(id+"F12.imprint","INTERSECT",VERTEX,{"derivedFrom":[subQ1,subQ0]});Q2=makeQuery(id+"F12.imprint","IMPRINT",FACE,{"disambiguationData":[TD([[makeQuery(id+"F12.imprint","IMPRINT",EDGE,{"disambiguationData":[TD([[subQ2,-1.0]])],"derivedFrom":subQ1}),1.0]])]});}
            extrude(context, id + "F21", {"entities" : qUnion([Q0, Q1, Q2]), "operationType" : NewBodyOperationType.ADD, "oppositeDirection" : true, "depth" : 30.96 * mm, "offsetDistance" : 25.4 * mm, "hasSecondDirection" : true, "secondDirectionOppositeDirection" : true, "secondDirectionDepth" : 26.2 * mm});
        }
        {
            var Q0;
            {var subQ1=sQuery(id+"F2.wireOp",EDGE,"E1.1");var subQ3=sQuery(id+"F2.wireOp",EDGE,"E2.left");var subQ9=sQuery(id+"F2.wireOp",EDGE,"E1.0");Q0=makeQuery(id+"F9.boolean.opBoolean","SPLIT",FACE,{"disambiguationData":[TD([makeQuery(id+"F4.opExtrude","SWEPT_FACE",FACE,{"disambiguationData":[OSD([subQ1])]})])],"derivedFrom":makeQuery(id+"F4.boolean.opBoolean","MERGE",FACE,{"derivedFrom":[makeQuery(id+"F3.opExtrude","SWEPT_FACE",FACE,{"disambiguationData":[OSD([subQ9,subQ3])]}),makeQuery(id+"F4.opExtrude","SWEPT_FACE",FACE,{"disambiguationData":[OSD([subQ9])]})]})});}
            var sketch = newSketch(context, id + "F22", { "sketchPlane" : qUnion([Q0])});
            skLineSegment(sketch, "E40.bottom", {"start": v(60.33, 1152.47) * mm, "end": v(168.28, 1152.47) * mm});
            skLineSegment(sketch, "E40.top", {"start": v(60.33, 1203.27) * mm, "end": v(168.28, 1203.27) * mm});
            skLineSegment(sketch, "E40.left", {"start": v(60.33, 1152.47) * mm, "end": v(60.33, 1203.27) * mm});
            skLineSegment(sketch, "E40.right", {"start": v(168.28, 1152.47) * mm, "end": v(168.28, 1203.27) * mm, "construction": true});
            skPoint(sketch, "E40.middle", {"position": v(114.3, 1177.87) * mm});
            skPoint(sketch, "E40.middle.positionSnap0", {"position": v(92.08, 1177.87) * mm});
            skPoint(sketch, "E40.centerSnap0", {"position": v(92.08, 1177.87) * mm});
            skLineSegment(sketch, "E41", {"start": v(92.08, 1203.27) * mm, "end": v(92.08, 1152.47) * mm});
            skPoint(sketch, "E42.end.orphan", {"position": v(168.28, 1177.87) * mm});
            skLineSegment(sketch, "E43", {"start": v(92.08, 1203.27) * mm, "end": v(168.28, 1177.87) * mm});
            skLineSegment(sketch, "E44", {"start": v(92.08, 1152.47) * mm, "end": v(168.28, 1177.87) * mm});
            skSolve(sketch);
        }
        {
            var Q0;
            {var subQ0=sQuery(id+"F22.wireOp",EDGE,"E43");Q0=makeQuery(id+"F22.imprint","IMPRINT",FACE,{"disambiguationData":[TD([[makeQuery(id+"F22.imprint","IMPRINT",EDGE,{"derivedFrom":subQ0}),-1.0]])]});}
            extrude(context, id + "F23", {"entities" : qUnion([Q0]), "oppositeDirection" : true, "depth" : 30.96 * mm, "offsetDistance" : 25.4 * mm, "hasSecondDirection" : true, "secondDirectionOppositeDirection" : true, "secondDirectionDepth" : 26.2 * mm});
        }
        {
            var Q0;
            Q0=makeQuery(id+"F23.opExtrude","CAP_EDGE",EDGE,{"disambiguationData":[OSD([sQuery(id+"F22.wireOp",EDGE,"E43")])],"isStart":true});
            var Q1;
            Q1=makeQuery(id+"F23.opExtrude","CAP_EDGE",EDGE,{"disambiguationData":[OSD([sQuery(id+"F22.wireOp",EDGE,"E43")])],"isStart":false});
            var Q2;
            Q2=makeQuery(id+"F23.opExtrude","CAP_EDGE",EDGE,{"disambiguationData":[OSD([sQuery(id+"F22.wireOp",EDGE,"E44")])],"isStart":true});
            var Q3;
            Q3=makeQuery(id+"F23.opExtrude","CAP_EDGE",EDGE,{"disambiguationData":[OSD([sQuery(id+"F22.wireOp",EDGE,"E44")])],"isStart":false});
            chamfer(context, id + "F24", {"entities" : qUnion([Q0, Q1, Q2, Q3]), "width" : 2.38 * mm});
        }
        {
            var Q0;
            {var subQ13=sQuery(id+"F22.wireOp",EDGE,"E40.top");var subQ15=sQuery(id+"F22.wireOp",EDGE,"E40.left");var subQ16=makeQuery(id+"F22.imprint","INTERSECT",VERTEX,{"derivedFrom":[subQ13,subQ15]});Q0=makeQuery(id+"F22.imprint","IMPRINT",FACE,{"disambiguationData":[TD([[makeQuery(id+"F22.imprint","IMPRINT",EDGE,{"disambiguationData":[TD([[subQ16,-1.0]])],"derivedFrom":subQ13}),-1.0]])]});}
            var Q1;
            {var subQ13=sQuery(id+"F22.wireOp",EDGE,"E40.bottom");var subQ15=sQuery(id+"F22.wireOp",EDGE,"E40.left");var subQ16=makeQuery(id+"F22.imprint","INTERSECT",VERTEX,{"derivedFrom":[subQ13,subQ15]});Q1=makeQuery(id+"F22.imprint","IMPRINT",FACE,{"disambiguationData":[TD([[makeQuery(id+"F22.imprint","IMPRINT",EDGE,{"disambiguationData":[TD([[subQ16,-1.0]])],"derivedFrom":subQ13}),1.0]])]});}
            var Q2;
            {var subQ1=sQuery(id+"F2.wireOp",EDGE,"E1.1");var subQ4=sQuery(id+"F2.wireOp",EDGE,"E2.left");var subQ10=sQuery(id+"F2.wireOp",EDGE,"E1.0");var subQ13=makeQuery(id+"F4.opExtrude","SWEPT_FACE",FACE,{"disambiguationData":[OSD([subQ1])]});var subQ14=makeQuery(id+"F4.opExtrude","SWEPT_FACE",FACE,{"disambiguationData":[OSD([subQ10])]});var subQ15=makeQuery(id+"F3.opExtrude","SWEPT_FACE",FACE,{"disambiguationData":[OSD([subQ10,subQ4])]});var subQ16=makeQuery(id+"F9.boolean.opBoolean","SPLIT",FACE,{"disambiguationData":[TD([subQ13])],"derivedFrom":makeQuery(id+"F4.boolean.opBoolean","MERGE",FACE,{"derivedFrom":[subQ15,subQ14]})});var subQ19=makeQuery(id+"F20.opChamfer","BLEND_EDGE",EDGE,{"blendedFrom":[makeQuery(id+"F4.opExtrude","CAP_EDGE",EDGE,{"disambiguationData":[OSD([subQ1])],"isStart":true}),subQ16],"blendedInto":[subQ16]});Q2=makeQuery(id+"F22.imprint","IMPRINT",FACE,{"disambiguationData":[TD([[makeQuery(id+"F22.imprint","IMPRINT",EDGE,{"derivedFrom":subQ19}),1.0]])]});}
            extrude(context, id + "F25", {"entities" : qUnion([Q0, Q1, Q2]), "operationType" : NewBodyOperationType.ADD, "oppositeDirection" : true, "depth" : 30.96 * mm, "offsetDistance" : 25.4 * mm, "hasSecondDirection" : true, "secondDirectionOppositeDirection" : true, "secondDirectionDepth" : 26.2 * mm});
        }
        {
            var Q0;
            {var subQ0=sQuery(id+"F22.wireOp",EDGE,"E41");Q0=makeQuery(id+"F25.boolean.opBoolean","MERGE",FACE,{"derivedFrom":[makeQuery(id+"F23.opExtrude","CAP_FACE",FACE,{"disambiguationData":[OSD([subQ0,sQuery(id+"F22.wireOp",EDGE,"E43"),sQuery(id+"F22.wireOp",EDGE,"E44")])],"isStart":true}),makeQuery(id+"F25.opExtrude","CAP_FACE",FACE,{"disambiguationData":[OSD([sQuery(id+"F22.wireOp",EDGE,"E40.bottom"),sQuery(id+"F22.wireOp",EDGE,"E40.top"),sQuery(id+"F22.wireOp",EDGE,"E40.left"),subQ0])],"isStart":true})]});}
            var sketch = newSketch(context, id + "F26", { "sketchPlane" : qUnion([Q0])});
            skLineSegment(sketch, "E45.bottom", {"start": v(92.08, 1162) * mm, "end": v(139.7, 1162) * mm});
            skLineSegment(sketch, "E45.top", {"start": v(92.08, 1193.74) * mm, "end": v(139.7, 1193.74) * mm});
            skLineSegment(sketch, "E45.left", {"start": v(92.08, 1162) * mm, "end": v(92.08, 1193.74) * mm});
            skLineSegment(sketch, "E45.right", {"start": v(139.7, 1162) * mm, "end": v(139.7, 1193.74) * mm, "construction": true});
            skPoint(sketch, "E45.middle", {"position": v(115.89, 1177.87) * mm});
            skLineSegment(sketch, "E46", {"start": v(92.08, 1193.74) * mm, "end": v(139.7, 1177.87) * mm});
            skLineSegment(sketch, "E47", {"start": v(139.7, 1177.87) * mm, "end": v(92.07, 1162) * mm});
            skSolve(sketch);
        }
        {
            var Q0;
            Q0 = qSketchRegion(id + "F26", true);
            extrude(context, id + "F27", {"entities" : qUnion([Q0]), "operationType" : NewBodyOperationType.ADD, "depth" : 3.17 * mm, "offsetDistance" : 25.4 * mm, "hasSecondDirection" : true, "secondDirectionOppositeDirection" : true, "secondDirectionDepth" : 7.94 * mm});
        }
        {
            var Q0;
            Q0=makeQuery(id+"F27.opExtrude","CAP_EDGE",EDGE,{"disambiguationData":[OSD([sQuery(id+"F26.wireOp",EDGE,"E46")])],"isStart":false});
            var Q1;
            Q1=makeQuery(id+"F27.opExtrude","CAP_EDGE",EDGE,{"disambiguationData":[OSD([sQuery(id+"F26.wireOp",EDGE,"E47")])],"isStart":false});
            var Q2;
            Q2=makeQuery(id+"F27.opExtrude","CAP_EDGE",EDGE,{"disambiguationData":[OSD([sQuery(id+"F26.wireOp",EDGE,"E46")])],"isStart":true});
            var Q3;
            Q3=makeQuery(id+"F27.opExtrude","CAP_EDGE",EDGE,{"disambiguationData":[OSD([sQuery(id+"F26.wireOp",EDGE,"E47")])],"isStart":true});
            chamfer(context, id + "F28", {"entities" : qUnion([Q0, Q1, Q2, Q3]), "width" : 3.17 * mm, "tangentPropagation" : true});
        }
        {
            var Q0;
            Q0=makeQuery(id+"F27.opExtrude","CAP_FACE",FACE,{"disambiguationData":[OSD([sQuery(id+"F26.wireOp",EDGE,"E45.left"),sQuery(id+"F26.wireOp",EDGE,"E46"),sQuery(id+"F26.wireOp",EDGE,"E47")])],"isStart":false});
            var sketch = newSketch(context, id + "F29", { "sketchPlane" : qUnion([Q0])});
            skLineSegment(sketch, "E48", {"start": v(92.08, 1187.05) * mm, "end": v(119.62, 1177.87) * mm, "construction": true});
            skLineSegment(sketch, "E49", {"start": v(119.62, 1177.87) * mm, "end": v(92.08, 1168.69) * mm, "construction": true});
            skCircle(sketch, "E50", {"center": v(114.6, 1177.87) * mm, "radius": 1.59 * mm});
            skLineSegment(sketch, "E51", {"start": v(114.6, 1177.87) * mm, "end": v(92.08, 1185.38) * mm, "construction": true});
            skLineSegment(sketch, "E52", {"start": v(114.6, 1177.87) * mm, "end": v(92.08, 1170.36) * mm, "construction": true});
            skLineSegment(sketch, "E53", {"start": v(114.6, 1177.87) * mm, "end": v(92.08, 1177.87) * mm, "construction": true});
            skCircle(sketch, "E54", {"center": v(96.6, 1171.86) * mm, "radius": 1.59 * mm});
            skCircle(sketch, "E55", {"center": v(96.6, 1183.87) * mm, "radius": 1.59 * mm});
            skCircle(sketch, "E56", {"center": v(103.34, 1177.87) * mm, "radius": 1.59 * mm});
            skSolve(sketch);
        }
        {
            var Q0;
            Q0=makeQuery(id+"F29.imprint","IMPRINT",FACE,{"disambiguationData":[TD([[makeQuery(id+"F29.imprint","IMPRINT",EDGE,{"derivedFrom":sQuery(id+"F29.wireOp",EDGE,"E54")}),1.0]])]});
            var Q1;
            Q1=makeQuery(id+"F29.imprint","IMPRINT",FACE,{"disambiguationData":[TD([[makeQuery(id+"F29.imprint","IMPRINT",EDGE,{"derivedFrom":sQuery(id+"F29.wireOp",EDGE,"E50")}),1.0]])]});
            var Q2;
            Q2=makeQuery(id+"F29.imprint","IMPRINT",FACE,{"disambiguationData":[TD([[makeQuery(id+"F29.imprint","IMPRINT",EDGE,{"derivedFrom":sQuery(id+"F29.wireOp",EDGE,"E55")}),1.0]])]});
            var Q3;
            Q3=makeQuery(id+"F29.imprint","IMPRINT",FACE,{"disambiguationData":[TD([[makeQuery(id+"F29.imprint","IMPRINT",EDGE,{"derivedFrom":sQuery(id+"F29.wireOp",EDGE,"E56")}),1.0]])]});
            extrude(context, id + "F30", {"entities" : qUnion([Q0, Q1, Q2, Q3]), "operationType" : NewBodyOperationType.ADD, "depth" : 0.8 * mm, "offsetDistance" : 25.4 * mm, "hasSecondDirection" : true, "secondDirectionOppositeDirection" : true, "secondDirectionDepth" : 11.9 * mm});
        }
    });
